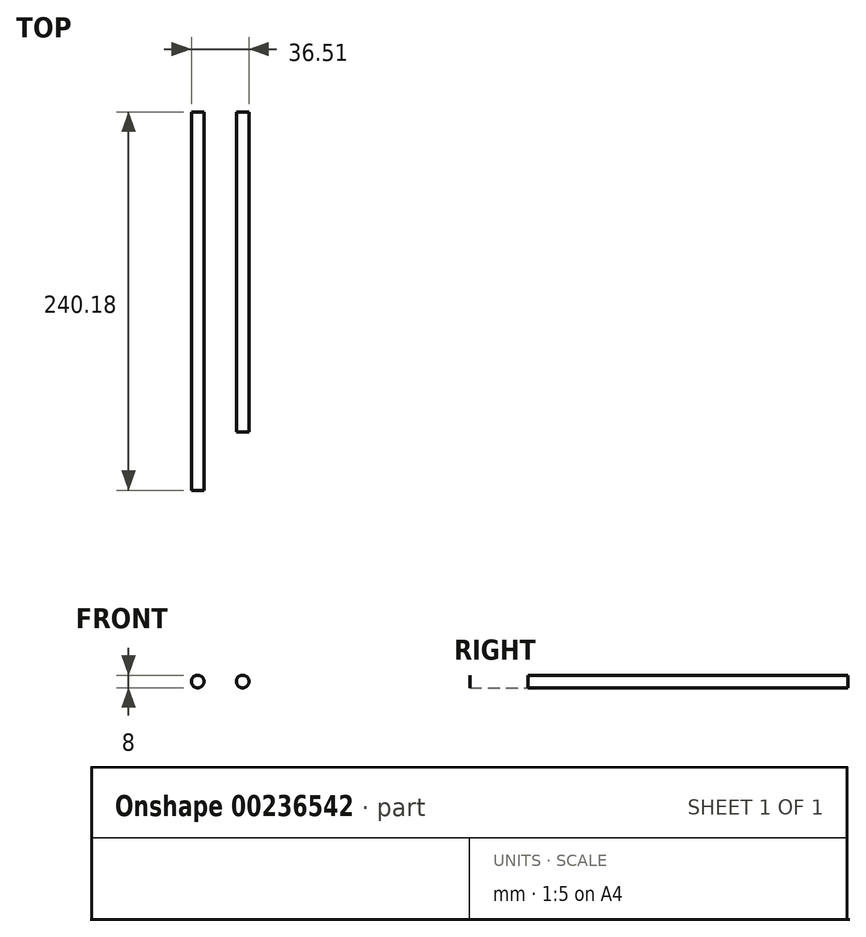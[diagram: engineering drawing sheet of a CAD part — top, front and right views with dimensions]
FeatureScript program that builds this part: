
annotation { "Feature Type Name" : "Feature", "Feature Type Description" : "" }
export const myFeature = defineFeature(function(context is Context, id is Id, definition is map)
    precondition{}
    {
        {
            var Q0;
            Q0=qCreatedBy(makeId("Front.planeOp"),FACE);
            var sketch = newSketch(context, id + "F0", { "sketchPlane" : qUnion([Q0])});
            skCircle(sketch, "E0", {"center": v(0, 0) * mm, "radius": 4 * mm});
            skSolve(sketch);
        }
        {
            var Q0;
            Q0 = qSketchRegion(id + "F0", true);
            extrude(context, id + "F1", {"entities" : qUnion([Q0]), "depth" : 203.2 * mm});
        }
        {
            var Q0;
            Q0=qCreatedBy(makeId("Front.planeOp"),FACE);
            var sketch = newSketch(context, id + "F2", { "sketchPlane" : qUnion([Q0])});
            skCircle(sketch, "E1", {"center": v(-28.5, 0) * mm, "radius": 4 * mm});
            skSolve(sketch);
        }
        {
            var Q0;
            Q0 = qSketchRegion(id + "F2", true);
            extrude(context, id + "F3", {"entities" : qUnion([Q0]), "depth" : 240.18 * mm});
        }
    });
